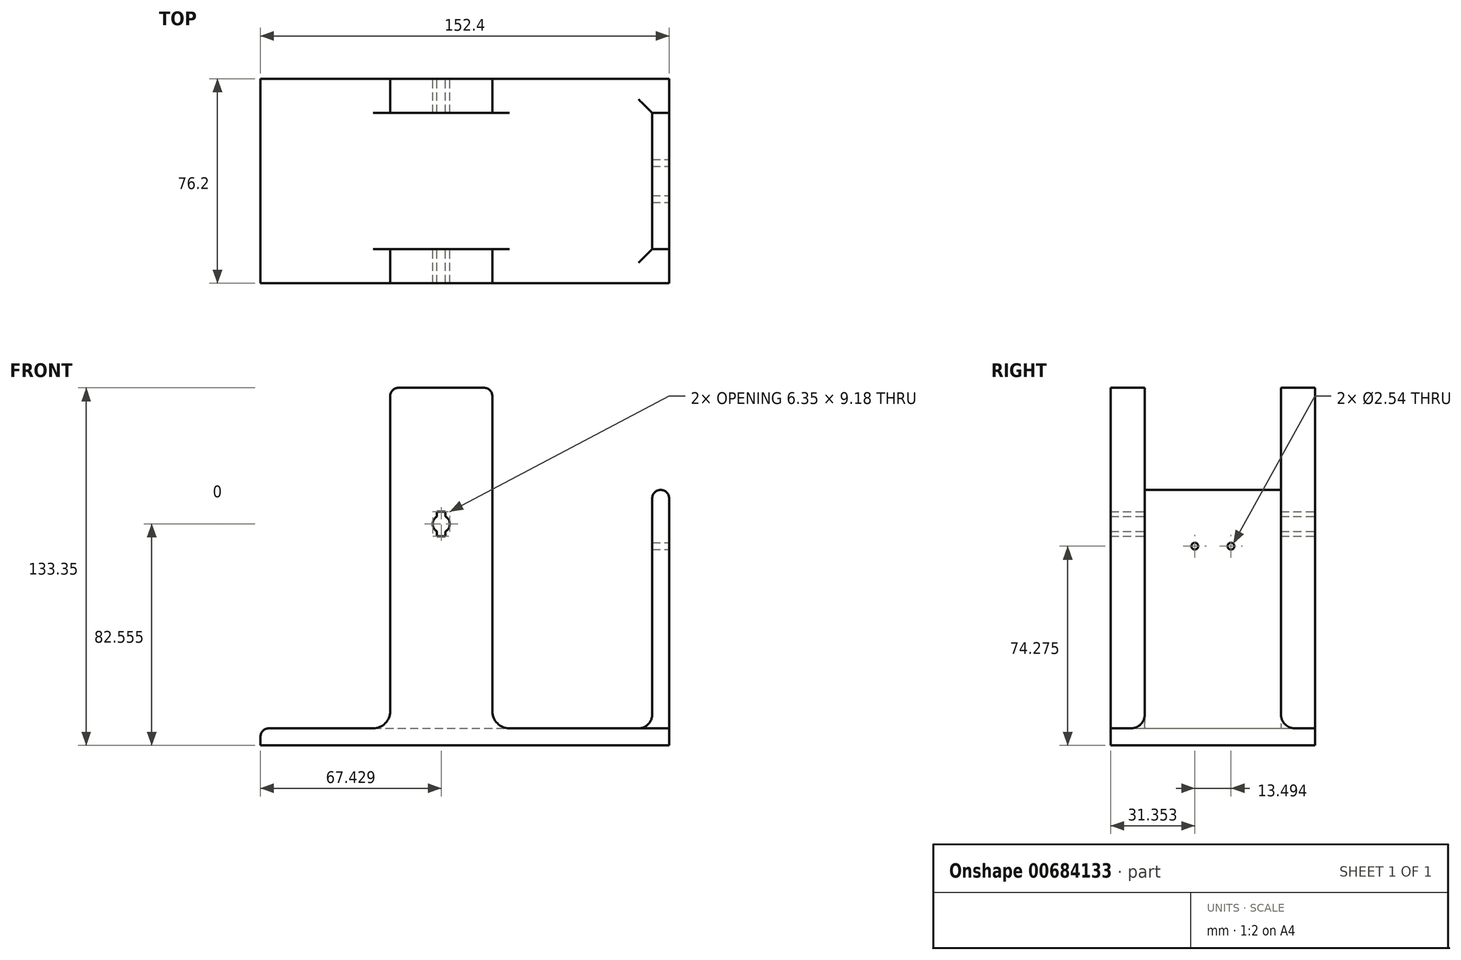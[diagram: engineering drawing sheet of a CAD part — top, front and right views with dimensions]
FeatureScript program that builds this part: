
annotation { "Feature Type Name" : "Feature", "Feature Type Description" : "" }
export const myFeature = defineFeature(function(context is Context, id is Id, definition is map)
    precondition{}
    {
        {
            var Q0;
            Q0=qCreatedBy(makeId("Front.planeOp"),FACE);
            var sketch = newSketch(context, id + "F0", { "sketchPlane" : qUnion([Q0])});
            skLineSegment(sketch, "E0", {"start": v(-74.9, -83.59) * mm, "end": v(77.5, -83.59) * mm});
            skLineSegment(sketch, "E1", {"start": v(77.5, -83.59) * mm, "end": v(77.5, -77.24) * mm});
            skLineSegment(sketch, "E2", {"start": v(71.15, -77.24) * mm, "end": v(17.93, -77.24) * mm});
            skLineSegment(sketch, "E3", {"start": v(11.58, -70.89) * mm, "end": v(11.58, 46.59) * mm});
            skLineSegment(sketch, "E4", {"start": v(8.4, 49.76) * mm, "end": v(-23.35, 49.76) * mm});
            skLineSegment(sketch, "E5", {"start": v(-26.52, 46.59) * mm, "end": v(-26.52, -70.89) * mm});
            skLineSegment(sketch, "E6", {"start": v(-32.87, -77.24) * mm, "end": v(-71.73, -77.24) * mm});
            skLineSegment(sketch, "E7", {"start": v(-74.9, -80.41) * mm, "end": v(-74.9, -83.59) * mm});
            skPoint(sketch, "E8.visualSharp", {"position": v(-26.52, -77.24) * mm});
            skArc(sketch, "E8.filletArc", {"start": v(-32.87, -77.24) * mm, "mid": v(-28.38, -75.38) * mm, "end": v(-26.52, -70.89) * mm});
            skPoint(sketch, "E9.visualSharp", {"position": v(11.58, -77.24) * mm});
            skArc(sketch, "E9.filletArc", {"start": v(11.58, -70.89) * mm, "mid": v(13.44, -75.38) * mm, "end": v(17.93, -77.24) * mm});
            skPoint(sketch, "E10.visualSharp", {"position": v(-26.52, 49.76) * mm});
            skArc(sketch, "E10.filletArc", {"start": v(-23.35, 49.76) * mm, "mid": v(-25.6, 48.84) * mm, "end": v(-26.52, 46.59) * mm});
            skPoint(sketch, "E11.visualSharp", {"position": v(11.58, 49.76) * mm});
            skArc(sketch, "E11.filletArc", {"start": v(11.58, 46.59) * mm, "mid": v(10.65, 48.84) * mm, "end": v(8.4, 49.76) * mm});
            skPoint(sketch, "E12.visualSharp", {"position": v(-74.9, -77.24) * mm});
            skArc(sketch, "E12.filletArc", {"start": v(-71.73, -77.24) * mm, "mid": v(-73.97, -78.16) * mm, "end": v(-74.9, -80.41) * mm});
            skLineSegment(sketch, "E13", {"start": v(-7.47, 49.76) * mm, "end": v(-7.47, -1.04) * mm, "construction": true});
            skLineSegment(sketch, "E14", {"start": v(-7.47, 11.66) * mm, "end": v(73.4, 11.66) * mm, "construction": true});
            skLineSegment(sketch, "E15", {"start": v(77.5, -77.24) * mm, "end": v(77.5, 11.66) * mm});
            skLineSegment(sketch, "E16", {"start": v(77.5, 11.66) * mm, "end": v(71.15, 11.66) * mm});
            skLineSegment(sketch, "E17", {"start": v(71.15, 11.66) * mm, "end": v(71.15, -77.24) * mm});
            skArc(sketch, "E18", {"start": v(-9.06, 1.71) * mm, "mid": v(-10.65, -1.04) * mm, "end": v(-9.06, -3.78) * mm});
            skLineSegment(sketch, "E19", {"start": v(-9.06, 1.71) * mm, "end": v(-9.06, 3.55) * mm, "construction": true});
            skLineSegment(sketch, "E20", {"start": v(-5.88, 1.71) * mm, "end": v(-5.88, 3.55) * mm});
            skLineSegment(sketch, "E21", {"start": v(-5.88, 3.55) * mm, "end": v(-9.06, 3.55) * mm});
            skLineSegment(sketch, "E22", {"start": v(-9.06, 1.71) * mm, "end": v(-9.06, 3.55) * mm});
            skLineSegment(sketch, "E23.trimOffspring", {"start": v(-5.88, 3.55) * mm, "end": v(-5.88, 1.71) * mm, "construction": true});
            skLineSegment(sketch, "E24", {"start": v(-7.47, -1.04) * mm, "end": v(-4.91, -1.04) * mm, "construction": true});
            skLineSegment(sketch, "E25.MirrorCS", {"start": v(-9.06, -3.78) * mm, "end": v(-9.06, -5.62) * mm});
            skLineSegment(sketch, "E26.MirrorCS", {"start": v(-5.88, -5.62) * mm, "end": v(-9.06, -5.62) * mm});
            skLineSegment(sketch, "E27.MirrorCS", {"start": v(-5.88, -5.62) * mm, "end": v(-5.88, -3.78) * mm});
            skArc(sketch, "E28.trimOffspring", {"start": v(-5.88, -3.78) * mm, "mid": v(-4.3, -1.04) * mm, "end": v(-5.88, 1.71) * mm});
            skSolve(sketch);
        }
        {
            var Q0;
            Q0 = qSketchRegion(id + "F0", true);
            extrude(context, id + "F1", {"entities" : qUnion([Q0]), "depth" : 76.2 * mm, "offsetDistance" : 25.4 * mm});
        }
        {
            var Q0;
            Q0=makeQuery(id+"F1.opExtrude","CAP_FACE",FACE,{"disambiguationData":[OSD([sQuery(id+"F0.wireOp",EDGE,"E0"),sQuery(id+"F0.wireOp",EDGE,"E1"),sQuery(id+"F0.wireOp",EDGE,"E2"),sQuery(id+"F0.wireOp",EDGE,"E3"),sQuery(id+"F0.wireOp",EDGE,"E4"),sQuery(id+"F0.wireOp",EDGE,"E5"),sQuery(id+"F0.wireOp",EDGE,"E6"),sQuery(id+"F0.wireOp",EDGE,"E7"),sQuery(id+"F0.wireOp",EDGE,"E8.filletArc"),sQuery(id+"F0.wireOp",EDGE,"E9.filletArc"),sQuery(id+"F0.wireOp",EDGE,"E10.filletArc"),sQuery(id+"F0.wireOp",EDGE,"E11.filletArc"),sQuery(id+"F0.wireOp",EDGE,"0bc6470b-84bb-4ac2-a3c3-4441ca9badd7.filletArc"),sQuery(id+"F0.wireOp",EDGE,"E12.filletArc")])],"isStart":true});
            cPlane(context, id + "F2", {"entities" : qUnion([Q0]), "cplaneType" : CPlaneType.OFFSET, "offset" : 12.7 * mm, "oppositeDirection" : true, "width" : 152.4 * mm, "height" : 152.4 * mm});
        }
        {
            var Q0;
            Q0=qCreatedBy(id+"F2.planeOp",FACE);
            var sketch = newSketch(context, id + "F3", { "sketchPlane" : qUnion([Q0])});
            skArc(sketch, "E29.0", {"start": v(32.87, -77.24) * mm, "mid": v(28.38, -75.38) * mm, "end": v(26.52, -70.89) * mm});
            skLineSegment(sketch, "E29.1", {"start": v(26.52, 46.59) * mm, "end": v(26.52, -70.89) * mm});
            skLineSegment(sketch, "E29.2", {"start": v(-8.4, 49.76) * mm, "end": v(23.35, 49.76) * mm});
            skArc(sketch, "E29.3", {"start": v(23.35, 49.76) * mm, "mid": v(25.6, 48.84) * mm, "end": v(26.52, 46.59) * mm});
            skArc(sketch, "E29.4", {"start": v(-11.58, 46.59) * mm, "mid": v(-10.65, 48.84) * mm, "end": v(-8.4, 49.76) * mm});
            skLineSegment(sketch, "E29.5", {"start": v(-11.58, -70.89) * mm, "end": v(-11.58, 46.59) * mm});
            skArc(sketch, "E29.6", {"start": v(-11.58, -70.89) * mm, "mid": v(-13.44, -75.38) * mm, "end": v(-17.93, -77.24) * mm});
            skLineSegment(sketch, "E30", {"start": v(32.87, -77.24) * mm, "end": v(-17.93, -77.24) * mm});
            skSolve(sketch);
        }
        {
            var Q0;
            Q0 = qSketchRegion(id + "F3", true);
            extrude(context, id + "F4", {"entities" : qUnion([Q0]), "operationType" : NewBodyOperationType.REMOVE, "endBound" : BoundingType.UP_TO_NEXT, "oppositeDirection" : true, "depth" : 25.4 * mm, "hasOffset" : true, "offsetDistance" : 12.7 * mm});
        }
        {
            var Q0;
            Q0=makeQuery(id+"F1.opExtrude","SWEPT_FACE",FACE,{"disambiguationData":[OSD([sQuery(id+"F0.wireOp",EDGE,"E1"),sQuery(id+"F0.wireOp",EDGE,"E15")])]});
            cPlane(context, id + "F5", {"entities" : qUnion([Q0]), "cplaneType" : CPlaneType.OFFSET, "offset" : 0 * mm, "width" : 152.4 * mm, "height" : 152.4 * mm});
        }
        {
            var Q0;
            Q0=qCreatedBy(id+"F5.planeOp",FACE);
            var sketch = newSketch(context, id + "F6", { "sketchPlane" : qUnion([Q0])});
            skLineSegment(sketch, "E31.0.0", {"start": v(0, -83.59) * mm, "end": v(0, 11.66) * mm});
            skLineSegment(sketch, "E31.0.1", {"start": v(0, 11.66) * mm, "end": v(-76.2, 11.66) * mm});
            skLineSegment(sketch, "E31.0.2", {"start": v(-76.2, 11.66) * mm, "end": v(-76.2, -83.59) * mm});
            skLineSegment(sketch, "E31.0.3", {"start": v(-76.2, -83.59) * mm, "end": v(0, -83.59) * mm});
            skLineSegment(sketch, "E32", {"start": v(-38.1, 11.66) * mm, "end": v(-38.1, -30.3) * mm, "construction": true});
            skLineSegment(sketch, "E33", {"start": v(-38.1, -30.3) * mm, "end": v(-24.6, -30.3) * mm, "construction": true});
            skLineSegment(sketch, "E34.MirrorCS", {"start": v(-38.1, -30.3) * mm, "end": v(-51.6, -30.3) * mm, "construction": true});
            skLineSegment(sketch, "E35", {"start": v(-51.6, -9.32) * mm, "end": v(-24.6, -9.32) * mm, "construction": true});
            skPoint(sketch, "E35.startSnap0", {"position": v(-38.1, -9.32) * mm});
            skLineSegment(sketch, "E36", {"start": v(-63.5, 11.66) * mm, "end": v(-63.5, -77.24) * mm});
            skLineSegment(sketch, "E37.MirrorCS", {"start": v(-12.7, 11.66) * mm, "end": v(-12.7, -77.24) * mm});
            skLineSegment(sketch, "E38", {"start": v(-76.2, -77.24) * mm, "end": v(0, -77.24) * mm});
            skPoint(sketch, "E39.end.orphan", {"position": v(-63.5, -77.24) * mm});
            skPoint(sketch, "E40", {"position": v(-31.35, -9.32) * mm});
            skPoint(sketch, "E41.MirrorP", {"position": v(-44.85, -9.32) * mm});
            skSolve(sketch);
        }
        {
            var Q0;
            Q0=sQuery(id+"F6.wireOp",VERTEX,"E41.MirrorP");
            var Q1;
            Q1=sQuery(id+"F6.wireOp",VERTEX,"E40");
            var Q2;
            Q2=makeQuery(id+"F1.opExtrude","SWEPT_BODY",BODY,{"disambiguationData":[OSD([sQuery(id+"F0.wireOp",EDGE,"E0"),sQuery(id+"F0.wireOp",EDGE,"E1"),sQuery(id+"F0.wireOp",EDGE,"E2"),sQuery(id+"F0.wireOp",EDGE,"E3"),sQuery(id+"F0.wireOp",EDGE,"E4"),sQuery(id+"F0.wireOp",EDGE,"E5"),sQuery(id+"F0.wireOp",EDGE,"E6"),sQuery(id+"F0.wireOp",EDGE,"E7"),sQuery(id+"F0.wireOp",EDGE,"E8.filletArc"),sQuery(id+"F0.wireOp",EDGE,"E9.filletArc"),sQuery(id+"F0.wireOp",EDGE,"E10.filletArc"),sQuery(id+"F0.wireOp",EDGE,"E11.filletArc"),sQuery(id+"F0.wireOp",EDGE,"E12.filletArc"),sQuery(id+"F0.wireOp",EDGE,"E15"),sQuery(id+"F0.wireOp",EDGE,"E16"),sQuery(id+"F0.wireOp",EDGE,"E17"),sQuery(id+"F0.wireOp",EDGE,"24e71776-fee4-4f32-ac67-4e2286a04322.filletArc"),sQuery(id+"F0.wireOp",EDGE,"E18"),sQuery(id+"F0.wireOp",EDGE,"E20"),sQuery(id+"F0.wireOp",EDGE,"E21"),sQuery(id+"F0.wireOp",EDGE,"E22")])]});
            hole(context, id + "F7", {"style" : HoleStyle.SIMPLE, "endStyle" : HoleEndStyle.THROUGH, "holeDiameter" : 2.54 * mm, "majorDiameter" : 6.35 * mm, "tappedDepth" : 8.9 * mm, "tapClearance" : 3, "locations" : qUnion([Q0, Q1]), "scope" : qUnion([Q2])});
        }
        {
            var Q0;
            {var subQ3=sQuery(id+"F6.wireOp",EDGE,"E36");Q0=makeQuery(id+"F6.imprint","IMPRINT",FACE,{"disambiguationData":[TD([[makeQuery(id+"F6.imprint","IMPRINT",EDGE,{"derivedFrom":subQ3}),-1.0]])]});}
            var Q1;
            {var subQ5=sQuery(id+"F6.wireOp",EDGE,"E37.MirrorCS");Q1=makeQuery(id+"F6.imprint","IMPRINT",FACE,{"disambiguationData":[TD([[makeQuery(id+"F6.imprint","IMPRINT",EDGE,{"derivedFrom":subQ5}),1.0]])]});}
            extrude(context, id + "F8", {"entities" : qUnion([Q0, Q1]), "operationType" : NewBodyOperationType.REMOVE, "oppositeDirection" : true, "depth" : 6.35 * mm, "offsetDistance" : 25.4 * mm});
        }
        {
            var Q0;
            Q0=makeQuery(id+"F8.boolean.opBoolean","COPY",EDGE,{"derivedFrom":makeQuery(id+"F8.opExtrude","SWEPT_EDGE",EDGE,{"disambiguationData":[OSD([sQuery(id+"F6.wireOp",EDGE,"E37.MirrorCS"),sQuery(id+"F6.wireOp",EDGE,"E38")])]})});
            var Q1;
            Q1=makeQuery(id+"F1.opExtrude","SWEPT_EDGE",EDGE,{"disambiguationData":[OSD([sQuery(id+"F0.wireOp",EDGE,"E2"),sQuery(id+"F0.wireOp",EDGE,"E17")])]});
            var Q2;
            Q2=makeQuery(id+"F8.boolean.opBoolean","COPY",EDGE,{"derivedFrom":makeQuery(id+"F8.opExtrude","SWEPT_EDGE",EDGE,{"disambiguationData":[OSD([sQuery(id+"F6.wireOp",EDGE,"E36"),sQuery(id+"F6.wireOp",EDGE,"E38")])]})});
            fillet(context, id + "F9", {"entities" : qUnion([Q0, Q1, Q2]), "radius" : 5.08 * mm, "tangentPropagation" : true, "allowEdgeOverflow" : false});
        }
        {
            var Q0;
            Q0=makeQuery(id+"F8.boolean.opBoolean","COPY",EDGE,{"derivedFrom":makeQuery(id+"F8.opExtrude","SWEPT_EDGE",EDGE,{"disambiguationData":[OSD([sQuery(id+"F6.wireOp",EDGE,"E31.0.1"),sQuery(id+"F6.wireOp",EDGE,"E36")])]})});
            var Q1;
            Q1=makeQuery(id+"F8.boolean.opBoolean","COPY",EDGE,{"derivedFrom":makeQuery(id+"F8.opExtrude","SWEPT_EDGE",EDGE,{"disambiguationData":[OSD([sQuery(id+"F6.wireOp",EDGE,"E31.0.1"),sQuery(id+"F6.wireOp",EDGE,"E37.MirrorCS")])]})});
            var Q2;
            Q2=makeQuery(id+"F1.opExtrude","SWEPT_EDGE",EDGE,{"disambiguationData":[OSD([sQuery(id+"F0.wireOp",EDGE,"E15"),sQuery(id+"F0.wireOp",EDGE,"E16")])]});
            var Q3;
            Q3=makeQuery(id+"F1.opExtrude","SWEPT_EDGE",EDGE,{"disambiguationData":[OSD([sQuery(id+"F0.wireOp",EDGE,"E16"),sQuery(id+"F0.wireOp",EDGE,"E17")])]});
            fillet(context, id + "F10", {"entities" : qUnion([Q0, Q1, Q2, Q3]), "radius" : 3.17 * mm, "tangentPropagation" : true, "allowEdgeOverflow" : false});
        }
    });
